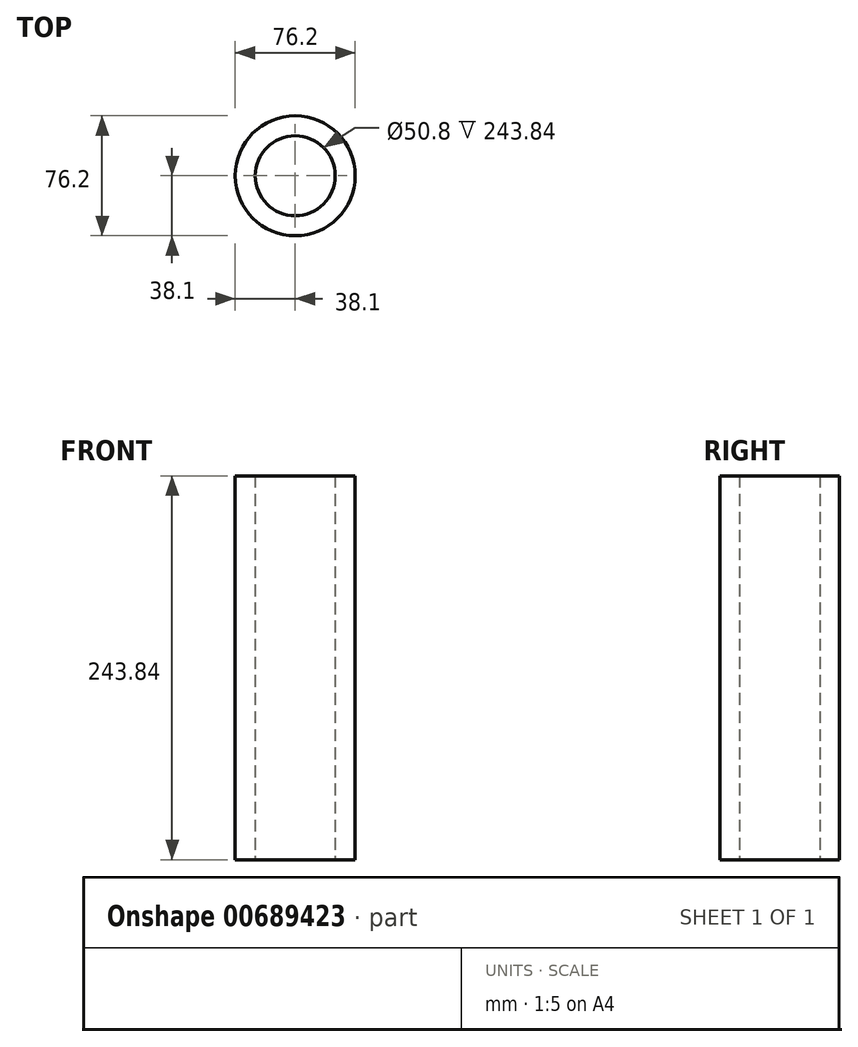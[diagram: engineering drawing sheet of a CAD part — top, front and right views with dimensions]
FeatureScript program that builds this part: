
annotation { "Feature Type Name" : "Feature", "Feature Type Description" : "" }
export const myFeature = defineFeature(function(context is Context, id is Id, definition is map)
    precondition{}
    {
        {
            var Q0;
            Q0=qCreatedBy(makeId("Top.planeOp"),FACE);
            var sketch = newSketch(context, id + "F0", { "sketchPlane" : qUnion([Q0])});
            skCircle(sketch, "E0", {"center": v(0, 0) * mm, "radius": 38.1 * mm});
            skCircle(sketch, "E1", {"center": v(0, 0) * mm, "radius": 25.4 * mm});
            skSolve(sketch);
        }
        {
            var Q0;
            Q0=makeQuery(id+"F0.imprint","IMPRINT",FACE,{"disambiguationData":[TD([[makeQuery(id+"F0.imprint","IMPRINT",EDGE,{"derivedFrom":sQuery(id+"F0.wireOp",EDGE,"E0")}),1.0]])]});
            extrude(context, id + "F1", {"entities" : qUnion([Q0]), "depth" : 243.84 * mm, "offsetDistance" : 25.4 * mm});
        }
    });
